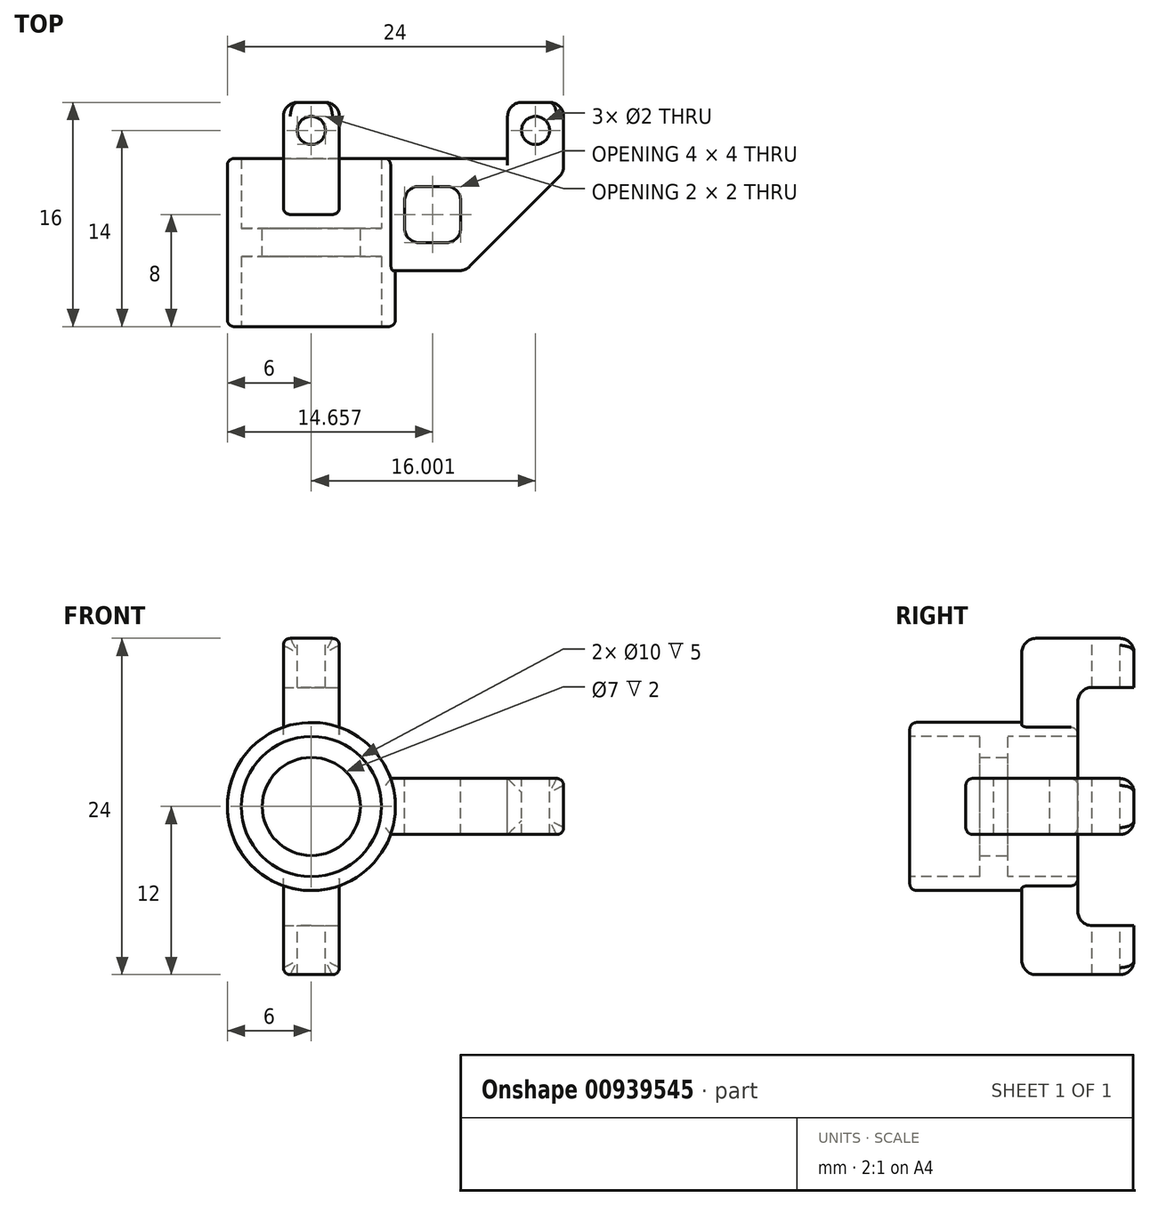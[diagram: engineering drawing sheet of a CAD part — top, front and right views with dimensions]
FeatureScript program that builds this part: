
annotation { "Feature Type Name" : "Feature", "Feature Type Description" : "" }
export const myFeature = defineFeature(function(context is Context, id is Id, definition is map)
    precondition{}
    {
        {
            var Q0;
            Q0=qCreatedBy(makeId("Front.planeOp"),FACE);
            var sketch = newSketch(context, id + "F0", { "sketchPlane" : qUnion([Q0])});
            skLineSegment(sketch, "E0.bottom", {"start": v(2, 12) * mm, "end": v(-2, 12) * mm});
            skLineSegment(sketch, "E0.top", {"start": v(2, -12) * mm, "end": v(-2, -12) * mm});
            skLineSegment(sketch, "E0.left", {"start": v(2, 12) * mm, "end": v(2, -12) * mm});
            skLineSegment(sketch, "E0.right", {"start": v(-2, 12) * mm, "end": v(-2, -12) * mm});
            skPoint(sketch, "E0.middle", {"position": v(0, 0) * mm});
            skSolve(sketch);
        }
        {
            var Q0;
            Q0 = qSketchRegion(id + "F0", true);
            extrude(context, id + "F1", {"entities" : qUnion([Q0]), "depth" : 4 * mm, "offsetDistance" : 25 * mm});
        }
        {
            var Q0;
            Q0=makeQuery(id+"F1.opExtrude","CAP_FACE",FACE,{"disambiguationData":[OSD([sQuery(id+"F0.wireOp",EDGE,"E0.bottom"),sQuery(id+"F0.wireOp",EDGE,"E0.top"),sQuery(id+"F0.wireOp",EDGE,"E0.left"),sQuery(id+"F0.wireOp",EDGE,"E0.right")])],"isStart":true});
            var sketch = newSketch(context, id + "F2", { "sketchPlane" : qUnion([Q0])});
            skLineSegment(sketch, "E1.bottom", {"start": v(2, -12) * mm, "end": v(-2, -12) * mm});
            skLineSegment(sketch, "E1.top", {"start": v(2, 12) * mm, "end": v(-2, 12) * mm});
            skLineSegment(sketch, "E1.left", {"start": v(2, -12) * mm, "end": v(2, 12) * mm});
            skLineSegment(sketch, "E1.right", {"start": v(-2, -12) * mm, "end": v(-2, 12) * mm});
            skPoint(sketch, "E1.middle", {"position": v(0, 0) * mm});
            skSolve(sketch);
        }
        {
            var Q0;
            Q0 = qSketchRegion(id + "F2", true);
            extrude(context, id + "F3", {"entities" : qUnion([Q0]), "operationType" : NewBodyOperationType.ADD, "depth" : 4 * mm, "offsetDistance" : 25 * mm});
        }
        {
            var Q0;
            Q0=qCreatedBy(makeId("Front.planeOp"),FACE);
            var sketch = newSketch(context, id + "F4", { "sketchPlane" : qUnion([Q0])});
            skLineSegment(sketch, "E2.bottom", {"start": v(0, 0) * mm, "end": v(18, 0) * mm});
            skLineSegment(sketch, "E2.top", {"start": v(0, 2) * mm, "end": v(18, 2) * mm});
            skLineSegment(sketch, "E2.left", {"start": v(0, 0) * mm, "end": v(0, 2) * mm});
            skLineSegment(sketch, "E2.right", {"start": v(18, 0) * mm, "end": v(18, 2) * mm});
            skLineSegment(sketch, "E3.top", {"start": v(0, -2) * mm, "end": v(18, -2) * mm});
            skLineSegment(sketch, "E3.left", {"start": v(0, 0) * mm, "end": v(0, -2) * mm});
            skLineSegment(sketch, "E3.right", {"start": v(18, 0) * mm, "end": v(18, -2) * mm});
            skSolve(sketch);
        }
        {
            var Q0;
            Q0 = qSketchRegion(id + "F4", true);
            extrude(context, id + "F5", {"entities" : qUnion([Q0]), "operationType" : NewBodyOperationType.ADD, "depth" : 8 * mm, "offsetDistance" : 25 * mm});
        }
        {
            var Q0;
            Q0=makeQuery(id+"F5.opExtrude","CAP_FACE",FACE,{"disambiguationData":[OSD([sQuery(id+"F4.wireOp",EDGE,"E2.top"),sQuery(id+"F4.wireOp",EDGE,"E2.left"),sQuery(id+"F4.wireOp",EDGE,"E2.right"),sQuery(id+"F4.wireOp",EDGE,"E3.top"),sQuery(id+"F4.wireOp",EDGE,"E3.left"),sQuery(id+"F4.wireOp",EDGE,"E3.right")])],"isStart":true});
            var sketch = newSketch(context, id + "F6", { "sketchPlane" : qUnion([Q0])});
            skLineSegment(sketch, "E4.bottom", {"start": v(-18, -2) * mm, "end": v(-14, -2) * mm});
            skLineSegment(sketch, "E4.top", {"start": v(-18, 2) * mm, "end": v(-14, 2) * mm});
            skLineSegment(sketch, "E4.left", {"start": v(-18, -2) * mm, "end": v(-18, 2) * mm});
            skLineSegment(sketch, "E4.right", {"start": v(-14, -2) * mm, "end": v(-14, 2) * mm});
            skSolve(sketch);
        }
        {
            var Q0;
            Q0 = qSketchRegion(id + "F6", true);
            extrude(context, id + "F7", {"entities" : qUnion([Q0]), "operationType" : NewBodyOperationType.ADD, "depth" : 4 * mm, "offsetDistance" : 25 * mm});
        }
        {
            var Q0;
            Q0=qCreatedBy(makeId("Front.planeOp"),FACE);
            var sketch = newSketch(context, id + "F8", { "sketchPlane" : qUnion([Q0])});
            skCircle(sketch, "E5", {"center": v(0, 0) * mm, "radius": 6 * mm});
            skSolve(sketch);
        }
        {
            var Q0;
            Q0 = qSketchRegion(id + "F8", true);
            extrude(context, id + "F9", {"entities" : qUnion([Q0]), "operationType" : NewBodyOperationType.ADD, "depth" : 12 * mm, "offsetDistance" : 25 * mm});
        }
        {
            var Q0;
            Q0=makeQuery(id+"F3.opExtrude","CAP_FACE",FACE,{"disambiguationData":[OSD([sQuery(id+"F2.wireOp",EDGE,"E1.bottom"),sQuery(id+"F2.wireOp",EDGE,"E1.top"),sQuery(id+"F2.wireOp",EDGE,"E1.left"),sQuery(id+"F2.wireOp",EDGE,"E1.right")])],"isStart":false});
            var sketch = newSketch(context, id + "F10", { "sketchPlane" : qUnion([Q0])});
            skCircle(sketch, "E6", {"center": v(0, 0) * mm, "radius": 3.5 * mm});
            skSolve(sketch);
        }
        {
            var Q0;
            Q0 = qSketchRegion(id + "F10", true);
            extrude(context, id + "F11", {"entities" : qUnion([Q0]), "operationType" : NewBodyOperationType.REMOVE, "oppositeDirection" : true, "depth" : 9 * mm, "offsetDistance" : 25 * mm});
        }
        {
            var Q0;
            Q0=makeQuery(id+"F9.opExtrude","CAP_FACE",FACE,{"disambiguationData":[OSD([sQuery(id+"F8.wireOp",EDGE,"E5")])],"isStart":false});
            var sketch = newSketch(context, id + "F12", { "sketchPlane" : qUnion([Q0])});
            skCircle(sketch, "E7", {"center": v(0, 0) * mm, "radius": 5 * mm});
            skSolve(sketch);
        }
        {
            var Q0;
            Q0 = qSketchRegion(id + "F12", true);
            extrude(context, id + "F13", {"entities" : qUnion([Q0]), "operationType" : NewBodyOperationType.REMOVE, "oppositeDirection" : true, "depth" : 5 * mm, "offsetDistance" : 25 * mm});
        }
        {
            var Q0;
            Q0=makeQuery(id+"F13.boolean.opBoolean","COPY",FACE,{"derivedFrom":makeQuery(id+"F13.opExtrude","CAP_FACE",FACE,{"disambiguationData":[OSD([sQuery(id+"F12.wireOp",EDGE,"E7")])],"isStart":false})});
            var sketch = newSketch(context, id + "F14", { "sketchPlane" : qUnion([Q0])});
            skCircle(sketch, "E8", {"center": v(0, 0) * mm, "radius": 3.5 * mm});
            skSolve(sketch);
        }
        {
            var Q0;
            Q0 = qSketchRegion(id + "F14", true);
            extrude(context, id + "F15", {"entities" : qUnion([Q0]), "operationType" : NewBodyOperationType.REMOVE, "oppositeDirection" : true, "depth" : 2 * mm, "offsetDistance" : 25 * mm});
        }
        {
            var Q0;
            Q0=qCreatedBy(makeId("Front.planeOp"),FACE);
            var sketch = newSketch(context, id + "F16", { "sketchPlane" : qUnion([Q0])});
            skCircle(sketch, "E9", {"center": v(0, 0) * mm, "radius": 5 * mm});
            skSolve(sketch);
        }
        {
            var Q0;
            Q0 = qSketchRegion(id + "F16", true);
            extrude(context, id + "F17", {"entities" : qUnion([Q0]), "operationType" : NewBodyOperationType.REMOVE, "oppositeDirection" : true, "depth" : 5 * mm, "offsetDistance" : 25 * mm});
        }
        {
            var Q0;
            Q0=qCreatedBy(makeId("Front.planeOp"),FACE);
            var sketch = newSketch(context, id + "F18", { "sketchPlane" : qUnion([Q0])});
            skCircle(sketch, "E10", {"center": v(0, 0) * mm, "radius": 5 * mm});
            skSolve(sketch);
        }
        {
            var Q0;
            Q0 = qSketchRegion(id + "F18", true);
            extrude(context, id + "F19", {"entities" : qUnion([Q0]), "operationType" : NewBodyOperationType.REMOVE, "depth" : 5 * mm, "offsetDistance" : 25 * mm});
        }
        {
            var Q0;
            Q0=qCreatedBy(makeId("Front.planeOp"),FACE);
            var sketch = newSketch(context, id + "F20", { "sketchPlane" : qUnion([Q0])});
            skLineSegment(sketch, "E11.bottom", {"start": v(-2, -8.5) * mm, "end": v(2, -8.5) * mm});
            skLineSegment(sketch, "E11.top", {"start": v(-2, 8.5) * mm, "end": v(2, 8.5) * mm});
            skLineSegment(sketch, "E11.left", {"start": v(-2, -8.5) * mm, "end": v(-2, 8.5) * mm});
            skLineSegment(sketch, "E11.right", {"start": v(2, -8.5) * mm, "end": v(2, 8.5) * mm});
            skPoint(sketch, "E11.middle", {"position": v(0, 0) * mm});
            skSolve(sketch);
        }
        {
            var Q0;
            Q0 = qSketchRegion(id + "F20", true);
            extrude(context, id + "F21", {"entities" : qUnion([Q0]), "operationType" : NewBodyOperationType.REMOVE, "oppositeDirection" : true, "depth" : 4 * mm, "offsetDistance" : 25 * mm});
        }
        {
            var Q0;
            Q0=makeQuery(id+"F5.opExtrude","CAP_EDGE",EDGE,{"disambiguationData":[OSD([sQuery(id+"F4.wireOp",EDGE,"E2.right"),sQuery(id+"F4.wireOp",EDGE,"E3.right")])],"isStart":false});
            chamfer(context, id + "F22", {"entities" : qUnion([Q0]), "width" : 7 * mm, "tangentPropagation" : true});
        }
        {
            var Q0;
            Q0=makeQuery(id+"F7.opExtrude","CAP_EDGE",EDGE,{"disambiguationData":[OSD([sQuery(id+"F6.wireOp",EDGE,"E4.left")])],"isStart":false});
            var Q1;
            Q1=makeQuery(id+"F3.opExtrude","CAP_EDGE",EDGE,{"disambiguationData":[OSD([sQuery(id+"F2.wireOp",EDGE,"E1.top")])],"isStart":false});
            var Q2;
            {var subQ0=sQuery(id+"F4.wireOp",EDGE,"E3.right");var subQ1=sQuery(id+"F4.wireOp",EDGE,"E2.right");Q2=makeQuery(id+"F22.opChamfer","BLEND_EDGE",EDGE,{"blendedFrom":[makeQuery(id+"F5.opExtrude","CAP_EDGE",EDGE,{"disambiguationData":[OSD([subQ1,subQ0])],"isStart":false}),makeQuery(id+"F5.opExtrude","CAP_FACE",FACE,{"disambiguationData":[OSD([sQuery(id+"F4.wireOp",EDGE,"E2.top"),sQuery(id+"F4.wireOp",EDGE,"E2.left"),subQ1,sQuery(id+"F4.wireOp",EDGE,"E3.top"),sQuery(id+"F4.wireOp",EDGE,"E3.left"),subQ0])],"isStart":false})],"blendedInto":[makeQuery(id+"F5.opExtrude","CAP_FACE",FACE,{"disambiguationData":[OSD([sQuery(id+"F4.wireOp",EDGE,"E2.top"),sQuery(id+"F4.wireOp",EDGE,"E2.left"),subQ1,sQuery(id+"F4.wireOp",EDGE,"E3.top"),sQuery(id+"F4.wireOp",EDGE,"E3.left"),subQ0])],"isStart":false})]});}
            var Q3;
            Q3=makeQuery(id+"F3.opExtrude","CAP_EDGE",EDGE,{"disambiguationData":[OSD([sQuery(id+"F2.wireOp",EDGE,"E1.bottom")])],"isStart":false});
            var Q4;
            Q4=makeQuery(id+"F21.boolean.opBoolean","COPY",EDGE,{"derivedFrom":makeQuery(id+"F21.opExtrude","CAP_EDGE",EDGE,{"disambiguationData":[OSD([sQuery(id+"F20.wireOp",EDGE,"E11.top")])],"isStart":false})});
            var Q5;
            Q5=makeQuery(id+"F21.boolean.opBoolean","COPY",EDGE,{"derivedFrom":makeQuery(id+"F21.opExtrude","CAP_EDGE",EDGE,{"disambiguationData":[OSD([sQuery(id+"F20.wireOp",EDGE,"E11.bottom")])],"isStart":false})});
            var Q6;
            {var subQ1=sQuery(id+"F2.wireOp",EDGE,"E1.right");Q6=makeQuery(id+"F11.boolean.opBoolean","SPLIT",EDGE,{"disambiguationData":[TD([makeQuery(id+"F1.opExtrude","SWEPT_FACE",FACE,{"disambiguationData":[OSD([sQuery(id+"F0.wireOp",EDGE,"E0.bottom")])]})])],"derivedFrom":makeQuery(id+"F3.opExtrude","CAP_EDGE",EDGE,{"disambiguationData":[OSD([subQ1])],"isStart":false})});}
            var Q7;
            {var subQ1=sQuery(id+"F2.wireOp",EDGE,"E1.left");Q7=makeQuery(id+"F11.boolean.opBoolean","SPLIT",EDGE,{"disambiguationData":[TD([makeQuery(id+"F1.opExtrude","SWEPT_FACE",FACE,{"disambiguationData":[OSD([sQuery(id+"F0.wireOp",EDGE,"E0.bottom")])]})])],"derivedFrom":makeQuery(id+"F3.opExtrude","CAP_EDGE",EDGE,{"disambiguationData":[OSD([subQ1])],"isStart":false})});}
            var Q8;
            {var subQ0=sQuery(id+"F2.wireOp",EDGE,"E1.right");Q8=makeQuery(id+"F11.boolean.opBoolean","SPLIT",EDGE,{"disambiguationData":[TD([makeQuery(id+"F1.opExtrude","SWEPT_FACE",FACE,{"disambiguationData":[OSD([sQuery(id+"F0.wireOp",EDGE,"E0.top")])]})])],"derivedFrom":makeQuery(id+"F3.opExtrude","CAP_EDGE",EDGE,{"disambiguationData":[OSD([subQ0])],"isStart":false})});}
            var Q9;
            {var subQ0=sQuery(id+"F2.wireOp",EDGE,"E1.left");Q9=makeQuery(id+"F11.boolean.opBoolean","SPLIT",EDGE,{"disambiguationData":[TD([makeQuery(id+"F1.opExtrude","SWEPT_FACE",FACE,{"disambiguationData":[OSD([sQuery(id+"F0.wireOp",EDGE,"E0.top")])]})])],"derivedFrom":makeQuery(id+"F3.opExtrude","CAP_EDGE",EDGE,{"disambiguationData":[OSD([subQ0])],"isStart":false})});}
            var Q10;
            Q10=makeQuery(id+"F7.opExtrude","CAP_EDGE",EDGE,{"disambiguationData":[OSD([sQuery(id+"F6.wireOp",EDGE,"E4.right")])],"isStart":false});
            var Q11;
            Q11=makeQuery(id+"F7.opExtrude","CAP_EDGE",EDGE,{"disambiguationData":[OSD([sQuery(id+"F6.wireOp",EDGE,"E4.top")])],"isStart":false});
            var Q12;
            Q12=makeQuery(id+"F7.opExtrude","CAP_EDGE",EDGE,{"disambiguationData":[OSD([sQuery(id+"F6.wireOp",EDGE,"E4.bottom")])],"isStart":false});
            var Q13;
            Q13=makeQuery(id+"F1.opExtrude","CAP_EDGE",EDGE,{"disambiguationData":[OSD([sQuery(id+"F0.wireOp",EDGE,"E0.bottom")])],"isStart":false});
            var Q14;
            Q14=makeQuery(id+"F1.opExtrude","CAP_EDGE",EDGE,{"disambiguationData":[OSD([sQuery(id+"F0.wireOp",EDGE,"E0.top")])],"isStart":false});
            var Q15;
            {var subQ0=sQuery(id+"F4.wireOp",EDGE,"E3.right");var subQ1=sQuery(id+"F4.wireOp",EDGE,"E2.right");Q15=makeQuery(id+"F22.opChamfer","BLEND_EDGE",EDGE,{"blendedFrom":[makeQuery(id+"F5.opExtrude","CAP_EDGE",EDGE,{"disambiguationData":[OSD([subQ1,subQ0])],"isStart":false}),makeQuery(id+"F7.boolean.opBoolean","MERGE",FACE,{"derivedFrom":[makeQuery(id+"F5.opExtrude","SWEPT_FACE",FACE,{"disambiguationData":[OSD([subQ1,subQ0])]}),makeQuery(id+"F7.opExtrude","SWEPT_FACE",FACE,{"disambiguationData":[OSD([sQuery(id+"F6.wireOp",EDGE,"E4.left")])]})]})],"blendedInto":[makeQuery(id+"F7.boolean.opBoolean","MERGE",FACE,{"derivedFrom":[makeQuery(id+"F5.opExtrude","SWEPT_FACE",FACE,{"disambiguationData":[OSD([subQ1,subQ0])]}),makeQuery(id+"F7.opExtrude","SWEPT_FACE",FACE,{"disambiguationData":[OSD([sQuery(id+"F6.wireOp",EDGE,"E4.left")])]})]})]});}
            var Q16;
            Q16=makeQuery(id+"F21.boolean.opBoolean","COPY",EDGE,{"derivedFrom":makeQuery(id+"F21.opExtrude","CAP_EDGE",EDGE,{"disambiguationData":[OSD([sQuery(id+"F20.wireOp",EDGE,"E11.top")])],"isStart":true})});
            var Q17;
            Q17=makeQuery(id+"F21.boolean.opBoolean","COPY",EDGE,{"derivedFrom":makeQuery(id+"F21.opExtrude","CAP_EDGE",EDGE,{"disambiguationData":[OSD([sQuery(id+"F20.wireOp",EDGE,"E11.bottom")])],"isStart":true})});
            var Q18;
            Q18=makeQuery(id+"F7.opExtrude","CAP_EDGE",EDGE,{"disambiguationData":[OSD([sQuery(id+"F6.wireOp",EDGE,"E4.right")])],"isStart":true});
            fillet(context, id + "F23", {"entities" : qUnion([Q0, Q1, Q2, Q3, Q4, Q5, Q6, Q7, Q8, Q9, Q10, Q11, Q12, Q13, Q14, Q15, Q16, Q17, Q18]), "radius" : 1 * mm, "tangentPropagation" : true, "allowEdgeOverflow" : false});
        }
        {
            var Q0;
            Q0=makeQuery(id+"F7.boolean.opBoolean","MERGE",FACE,{"derivedFrom":[makeQuery(id+"F5.opExtrude","SWEPT_FACE",FACE,{"disambiguationData":[OSD([sQuery(id+"F4.wireOp",EDGE,"E2.top")])]}),makeQuery(id+"F7.opExtrude","SWEPT_FACE",FACE,{"disambiguationData":[OSD([sQuery(id+"F6.wireOp",EDGE,"E4.top")])]})]});
            var sketch = newSketch(context, id + "F24", { "sketchPlane" : qUnion([Q0])});
            skLineSegment(sketch, "E12.bottom", {"start": v(6.66, -2) * mm, "end": v(10.66, -2) * mm});
            skLineSegment(sketch, "E12.top", {"start": v(6.66, -6) * mm, "end": v(10.66, -6) * mm});
            skLineSegment(sketch, "E12.left", {"start": v(6.66, -2) * mm, "end": v(6.66, -6) * mm});
            skLineSegment(sketch, "E12.right", {"start": v(10.66, -2) * mm, "end": v(10.66, -6) * mm});
            skPoint(sketch, "E12.middle", {"position": v(8.66, -4) * mm});
            skSolve(sketch);
        }
        {
            var Q0;
            Q0 = qSketchRegion(id + "F24", true);
            extrude(context, id + "F25", {"entities" : qUnion([Q0]), "operationType" : NewBodyOperationType.REMOVE, "oppositeDirection" : true, "depth" : 4 * mm, "offsetDistance" : 25 * mm});
        }
        {
            var Q0;
            Q0=makeQuery(id+"F25.boolean.opBoolean","COPY",EDGE,{"derivedFrom":makeQuery(id+"F25.opExtrude","SWEPT_EDGE",EDGE,{"disambiguationData":[OSD([sQuery(id+"F24.wireOp",EDGE,"E12.bottom"),sQuery(id+"F24.wireOp",EDGE,"E12.left")])]})});
            var Q1;
            Q1=makeQuery(id+"F25.boolean.opBoolean","COPY",EDGE,{"derivedFrom":makeQuery(id+"F25.opExtrude","SWEPT_EDGE",EDGE,{"disambiguationData":[OSD([sQuery(id+"F24.wireOp",EDGE,"E12.bottom"),sQuery(id+"F24.wireOp",EDGE,"E12.right")])]})});
            var Q2;
            Q2=makeQuery(id+"F25.boolean.opBoolean","COPY",EDGE,{"derivedFrom":makeQuery(id+"F25.opExtrude","SWEPT_EDGE",EDGE,{"disambiguationData":[OSD([sQuery(id+"F24.wireOp",EDGE,"E12.top"),sQuery(id+"F24.wireOp",EDGE,"E12.right")])]})});
            var Q3;
            Q3=makeQuery(id+"F25.boolean.opBoolean","COPY",EDGE,{"derivedFrom":makeQuery(id+"F25.opExtrude","SWEPT_EDGE",EDGE,{"disambiguationData":[OSD([sQuery(id+"F24.wireOp",EDGE,"E12.top"),sQuery(id+"F24.wireOp",EDGE,"E12.left")])]})});
            fillet(context, id + "F26", {"entities" : qUnion([Q0, Q1, Q2, Q3]), "radius" : 1 * mm, "tangentPropagation" : true, "allowEdgeOverflow" : false});
        }
        {
            var Q0;
            Q0=makeQuery(id+"F3.boolean.opBoolean","MERGE",FACE,{"derivedFrom":[makeQuery(id+"F1.opExtrude","SWEPT_FACE",FACE,{"disambiguationData":[OSD([sQuery(id+"F0.wireOp",EDGE,"E0.bottom")])]}),makeQuery(id+"F3.opExtrude","SWEPT_FACE",FACE,{"disambiguationData":[OSD([sQuery(id+"F2.wireOp",EDGE,"E1.top")])]})]});
            var sketch = newSketch(context, id + "F27", { "sketchPlane" : qUnion([Q0])});
            skCircle(sketch, "E13", {"center": v(0, 2) * mm, "radius": 1 * mm});
            skSolve(sketch);
        }
        {
            var Q0;
            Q0 = qSketchRegion(id + "F27", true);
            extrude(context, id + "F28", {"entities" : qUnion([Q0]), "operationType" : NewBodyOperationType.REMOVE, "oppositeDirection" : true, "depth" : 26 * mm, "offsetDistance" : 25 * mm});
        }
        {
            var Q0;
            Q0=makeQuery(id+"F7.boolean.opBoolean","MERGE",FACE,{"derivedFrom":[makeQuery(id+"F5.opExtrude","SWEPT_FACE",FACE,{"disambiguationData":[OSD([sQuery(id+"F4.wireOp",EDGE,"E2.top")])]}),makeQuery(id+"F7.opExtrude","SWEPT_FACE",FACE,{"disambiguationData":[OSD([sQuery(id+"F6.wireOp",EDGE,"E4.top")])]})]});
            var sketch = newSketch(context, id + "F29", { "sketchPlane" : qUnion([Q0])});
            skCircle(sketch, "E14", {"center": v(16, 2) * mm, "radius": 1 * mm});
            skSolve(sketch);
        }
        {
            var Q0;
            Q0 = qSketchRegion(id + "F29", true);
            extrude(context, id + "F30", {"entities" : qUnion([Q0]), "operationType" : NewBodyOperationType.REMOVE, "oppositeDirection" : true, "depth" : 4 * mm, "offsetDistance" : 25 * mm});
        }
        {
            var Q0;
            Q0=makeQuery(id+"F9.opExtrude","CAP_EDGE",EDGE,{"disambiguationData":[OSD([sQuery(id+"F8.wireOp",EDGE,"E5")])],"isStart":false});
            fillet(context, id + "F31", {"entities" : qUnion([Q0]), "radius" : .5 * mm, "tangentPropagation" : true, "allowEdgeOverflow" : false});
        }
        {
            var Q0;
            Q0=makeQuery(id+"F22.opChamfer","BLEND_EDGE",EDGE,{"blendedFrom":[makeQuery(id+"F5.opExtrude","CAP_EDGE",EDGE,{"disambiguationData":[OSD([sQuery(id+"F4.wireOp",EDGE,"E2.right"),sQuery(id+"F4.wireOp",EDGE,"E3.right")])],"isStart":false}),makeQuery(id+"F7.boolean.opBoolean","MERGE",FACE,{"derivedFrom":[makeQuery(id+"F5.opExtrude","SWEPT_FACE",FACE,{"disambiguationData":[OSD([sQuery(id+"F4.wireOp",EDGE,"E2.top")])]}),makeQuery(id+"F7.opExtrude","SWEPT_FACE",FACE,{"disambiguationData":[OSD([sQuery(id+"F6.wireOp",EDGE,"E4.top")])]})]})],"blendedInto":[makeQuery(id+"F7.boolean.opBoolean","MERGE",FACE,{"derivedFrom":[makeQuery(id+"F5.opExtrude","SWEPT_FACE",FACE,{"disambiguationData":[OSD([sQuery(id+"F4.wireOp",EDGE,"E2.top")])]}),makeQuery(id+"F7.opExtrude","SWEPT_FACE",FACE,{"disambiguationData":[OSD([sQuery(id+"F6.wireOp",EDGE,"E4.top")])]})]})]});
            fillet(context, id + "F32", {"entities" : qUnion([Q0]), "radius" : .5 * mm, "tangentPropagation" : true, "allowEdgeOverflow" : false});
        }
        {
            var Q0;
            Q0=makeQuery(id+"F22.opChamfer","BLEND_EDGE",EDGE,{"blendedFrom":[makeQuery(id+"F5.opExtrude","CAP_EDGE",EDGE,{"disambiguationData":[OSD([sQuery(id+"F4.wireOp",EDGE,"E2.right"),sQuery(id+"F4.wireOp",EDGE,"E3.right")])],"isStart":false}),makeQuery(id+"F7.boolean.opBoolean","MERGE",FACE,{"derivedFrom":[makeQuery(id+"F5.opExtrude","SWEPT_FACE",FACE,{"disambiguationData":[OSD([sQuery(id+"F4.wireOp",EDGE,"E3.top")])]}),makeQuery(id+"F7.opExtrude","SWEPT_FACE",FACE,{"disambiguationData":[OSD([sQuery(id+"F6.wireOp",EDGE,"E4.bottom")])]})]})],"blendedInto":[makeQuery(id+"F7.boolean.opBoolean","MERGE",FACE,{"derivedFrom":[makeQuery(id+"F5.opExtrude","SWEPT_FACE",FACE,{"disambiguationData":[OSD([sQuery(id+"F4.wireOp",EDGE,"E3.top")])]}),makeQuery(id+"F7.opExtrude","SWEPT_FACE",FACE,{"disambiguationData":[OSD([sQuery(id+"F6.wireOp",EDGE,"E4.bottom")])]})]})]});
            fillet(context, id + "F33", {"entities" : qUnion([Q0]), "radius" : .5 * mm, "tangentPropagation" : true, "allowEdgeOverflow" : false});
        }
        {
            var Q0;
            {var subQ0=sQuery(id+"F0.wireOp",EDGE,"E0.right");var subQ1=sQuery(id+"F0.wireOp",EDGE,"E0.bottom");Q0=makeQuery(id+"F9.boolean.opBoolean","SPLIT",EDGE,{"disambiguationData":[TD([makeQuery(id+"F1.opExtrude","SWEPT_FACE",FACE,{"disambiguationData":[OSD([subQ1])]})])],"derivedFrom":makeQuery(id+"F1.opExtrude","CAP_EDGE",EDGE,{"disambiguationData":[OSD([subQ0])],"isStart":false})});}
            var Q1;
            Q1=makeQuery(id+"F21.boolean.opBoolean","COPY",EDGE,{"derivedFrom":makeQuery(id+"F21.opExtrude","SWEPT_EDGE",EDGE,{"disambiguationData":[OSD([sQuery(id+"F20.wireOp",EDGE,"E11.top"),sQuery(id+"F20.wireOp",EDGE,"E11.right")])]})});
            var Q2;
            {var subQ0=sQuery(id+"F0.wireOp",EDGE,"E0.left");var subQ1=sQuery(id+"F0.wireOp",EDGE,"E0.bottom");Q2=makeQuery(id+"F5.boolean.opBoolean","SPLIT",EDGE,{"disambiguationData":[TD([makeQuery(id+"F1.opExtrude","SWEPT_FACE",FACE,{"disambiguationData":[OSD([subQ1])]})])],"derivedFrom":makeQuery(id+"F1.opExtrude","CAP_EDGE",EDGE,{"disambiguationData":[OSD([subQ0])],"isStart":false})});}
            fillet(context, id + "F34", {"entities" : qUnion([Q0, Q1, Q2]), "radius" : .5 * mm, "tangentPropagation" : true, "allowEdgeOverflow" : false});
        }
        {
            var Q0;
            {var subQ0=sQuery(id+"F0.wireOp",EDGE,"E0.right");var subQ1=sQuery(id+"F0.wireOp",EDGE,"E0.top");Q0=makeQuery(id+"F9.boolean.opBoolean","SPLIT",EDGE,{"disambiguationData":[TD([makeQuery(id+"F1.opExtrude","SWEPT_FACE",FACE,{"disambiguationData":[OSD([subQ1])]})])],"derivedFrom":makeQuery(id+"F1.opExtrude","CAP_EDGE",EDGE,{"disambiguationData":[OSD([subQ0])],"isStart":false})});}
            var Q1;
            {var subQ0=sQuery(id+"F0.wireOp",EDGE,"E0.left");var subQ1=sQuery(id+"F0.wireOp",EDGE,"E0.top");Q1=makeQuery(id+"F5.boolean.opBoolean","SPLIT",EDGE,{"disambiguationData":[TD([makeQuery(id+"F1.opExtrude","SWEPT_FACE",FACE,{"disambiguationData":[OSD([subQ1])]})])],"derivedFrom":makeQuery(id+"F1.opExtrude","CAP_EDGE",EDGE,{"disambiguationData":[OSD([subQ0])],"isStart":false})});}
            var Q2;
            {var subQ1=sQuery(id+"F20.wireOp",EDGE,"E11.bottom");var subQ2=sQuery(id+"F20.wireOp",EDGE,"E11.left");Q2=makeQuery(id+"F21.boolean.opBoolean","COPY",EDGE,{"disambiguationData":[TD([makeQuery(id+"F21.opExtrude","SWEPT_FACE",FACE,{"disambiguationData":[OSD([subQ1])]})])],"derivedFrom":makeQuery(id+"F21.opExtrude","CAP_EDGE",EDGE,{"disambiguationData":[OSD([subQ2])],"isStart":true})});}
            var Q3;
            {var subQ1=sQuery(id+"F20.wireOp",EDGE,"E11.top");var subQ2=sQuery(id+"F20.wireOp",EDGE,"E11.left");Q3=makeQuery(id+"F21.boolean.opBoolean","COPY",EDGE,{"disambiguationData":[TD([makeQuery(id+"F21.opExtrude","SWEPT_FACE",FACE,{"disambiguationData":[OSD([subQ1])]})])],"derivedFrom":makeQuery(id+"F21.opExtrude","CAP_EDGE",EDGE,{"disambiguationData":[OSD([subQ2])],"isStart":true})});}
            fillet(context, id + "F35", {"entities" : qUnion([Q0, Q1, Q2, Q3]), "radius" : .5 * mm, "tangentPropagation" : true, "allowEdgeOverflow" : false});
        }
        {
            var Q0;
            {var subQ1=sQuery(id+"F20.wireOp",EDGE,"E11.bottom");var subQ2=sQuery(id+"F20.wireOp",EDGE,"E11.right");Q0=makeQuery(id+"F21.boolean.opBoolean","COPY",EDGE,{"disambiguationData":[TD([makeQuery(id+"F21.opExtrude","SWEPT_FACE",FACE,{"disambiguationData":[OSD([subQ1])]})])],"derivedFrom":makeQuery(id+"F21.opExtrude","CAP_EDGE",EDGE,{"disambiguationData":[OSD([subQ2])],"isStart":true})});}
            var Q1;
            Q1=makeQuery(id+"F5.opExtrude","CAP_EDGE",EDGE,{"disambiguationData":[OSD([sQuery(id+"F4.wireOp",EDGE,"E2.top")])],"isStart":true});
            var Q2;
            Q2=makeQuery(id+"F5.opExtrude","CAP_EDGE",EDGE,{"disambiguationData":[OSD([sQuery(id+"F4.wireOp",EDGE,"E3.top")])],"isStart":true});
            fillet(context, id + "F36", {"entities" : qUnion([Q0, Q1, Q2]), "radius" : .5 * mm, "tangentPropagation" : true, "allowEdgeOverflow" : false});
        }
        {
            var Q0;
            {var subQ0=sQuery(id+"F4.wireOp",EDGE,"E2.top");var subQ1=sQuery(id+"F8.wireOp",EDGE,"E5");var subQ2=makeQuery(id+"F9.opExtrude","CAP_FACE",FACE,{"disambiguationData":[OSD([subQ1])],"isStart":true});var subQ3=makeQuery(id+"F5.opExtrude","CAP_FACE",FACE,{"disambiguationData":[OSD([subQ0,sQuery(id+"F4.wireOp",EDGE,"E2.left"),sQuery(id+"F4.wireOp",EDGE,"E2.right"),sQuery(id+"F4.wireOp",EDGE,"E3.top"),sQuery(id+"F4.wireOp",EDGE,"E3.left"),sQuery(id+"F4.wireOp",EDGE,"E3.right")])],"isStart":true});var subQ4=makeQuery(id+"F9.opExtrude","SWEPT_FACE",FACE,{"disambiguationData":[OSD([subQ1])]});Q0=makeQuery(id+"F9.boolean.opBoolean","SPLIT",EDGE,{"disambiguationData":[topologyDisambiguationEdgeConnected([subQ3,subQ4,subQ2]),TD([makeQuery(id+"F5.opExtrude","SWEPT_FACE",FACE,{"disambiguationData":[OSD([subQ0])]})])],"derivedFrom":makeQuery(id+"F9.opExtrude","CAP_EDGE",EDGE,{"disambiguationData":[OSD([subQ1])],"isStart":true})});}
            fillet(context, id + "F37", {"entities" : qUnion([Q0]), "radius" : .5 * mm, "tangentPropagation" : true, "allowEdgeOverflow" : false});
        }
        {
            var Q0;
            {var subQ0=sQuery(id+"F8.wireOp",EDGE,"E5");Q0=makeQuery(id+"F9.boolean.opBoolean","SPLIT",EDGE,{"disambiguationData":[topologyDisambiguationEdgeConnected([makeQuery(id+"F9.opExtrude","SWEPT_FACE",FACE,{"disambiguationData":[OSD([subQ0])]}),makeQuery(id+"F9.opExtrude","CAP_FACE",FACE,{"disambiguationData":[OSD([subQ0])],"isStart":true})])],"derivedFrom":makeQuery(id+"F9.opExtrude","CAP_EDGE",EDGE,{"disambiguationData":[OSD([subQ0])],"isStart":true})});}
            var Q1;
            {var subQ0=sQuery(id+"F4.wireOp",EDGE,"E3.top");var subQ1=makeQuery(id+"F5.opExtrude","CAP_FACE",FACE,{"disambiguationData":[OSD([sQuery(id+"F4.wireOp",EDGE,"E2.top"),sQuery(id+"F4.wireOp",EDGE,"E2.left"),sQuery(id+"F4.wireOp",EDGE,"E2.right"),subQ0,sQuery(id+"F4.wireOp",EDGE,"E3.left"),sQuery(id+"F4.wireOp",EDGE,"E3.right")])],"isStart":true});var subQ2=sQuery(id+"F8.wireOp",EDGE,"E5");var subQ3=makeQuery(id+"F9.opExtrude","CAP_FACE",FACE,{"disambiguationData":[OSD([subQ2])],"isStart":true});var subQ4=makeQuery(id+"F9.opExtrude","SWEPT_FACE",FACE,{"disambiguationData":[OSD([subQ2])]});Q1=makeQuery(id+"F9.boolean.opBoolean","SPLIT",EDGE,{"disambiguationData":[topologyDisambiguationEdgeConnected([subQ1,subQ4,subQ3]),TD([makeQuery(id+"F5.opExtrude","SWEPT_FACE",FACE,{"disambiguationData":[OSD([subQ0])]})])],"derivedFrom":makeQuery(id+"F9.opExtrude","CAP_EDGE",EDGE,{"disambiguationData":[OSD([subQ2])],"isStart":true})});}
            fillet(context, id + "F38", {"entities" : qUnion([Q0, Q1]), "radius" : .5 * mm, "tangentPropagation" : true, "allowEdgeOverflow" : false});
        }
    });
